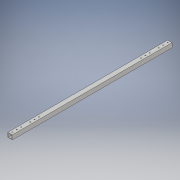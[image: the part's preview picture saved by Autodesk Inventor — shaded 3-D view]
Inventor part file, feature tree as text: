
AUTODESK INVENTOR PART (.ipt)
format: ipt  version: 2018 (Build 220112000, 112)  size: 140,800 bytes
history: native  units: in
note: dims shown in document units (in); Inventor stores cm internally (conversion verified against a paired STEP export)
features: extrude x2, sketch x2
ambient origin geometry x8: Origin, YZ Plane, XZ Plane, XY Plane, X Axis, Y Axis, Z Axis, Center Point
bodies: Solid1 (feature_tree)
feature tree (4):
  extrude  "Extrusion1"  Depth=1.0in
  extrude  "Extrusion2"  Depth=36.0in TaperAngle=0.0deg
  sketch  "Sketch1"  dims[d0=1.0in d1=1.0in]
  sketch  "Sketch2"  dims[d2=0.125in d3=36.0in d4=0.0in d5=0.5in d6=1.0in d7=1.0in d8=5.5in d9=1.0in d10=2.0in d11=0.2031in d12=36.0in d13=0.0in]
